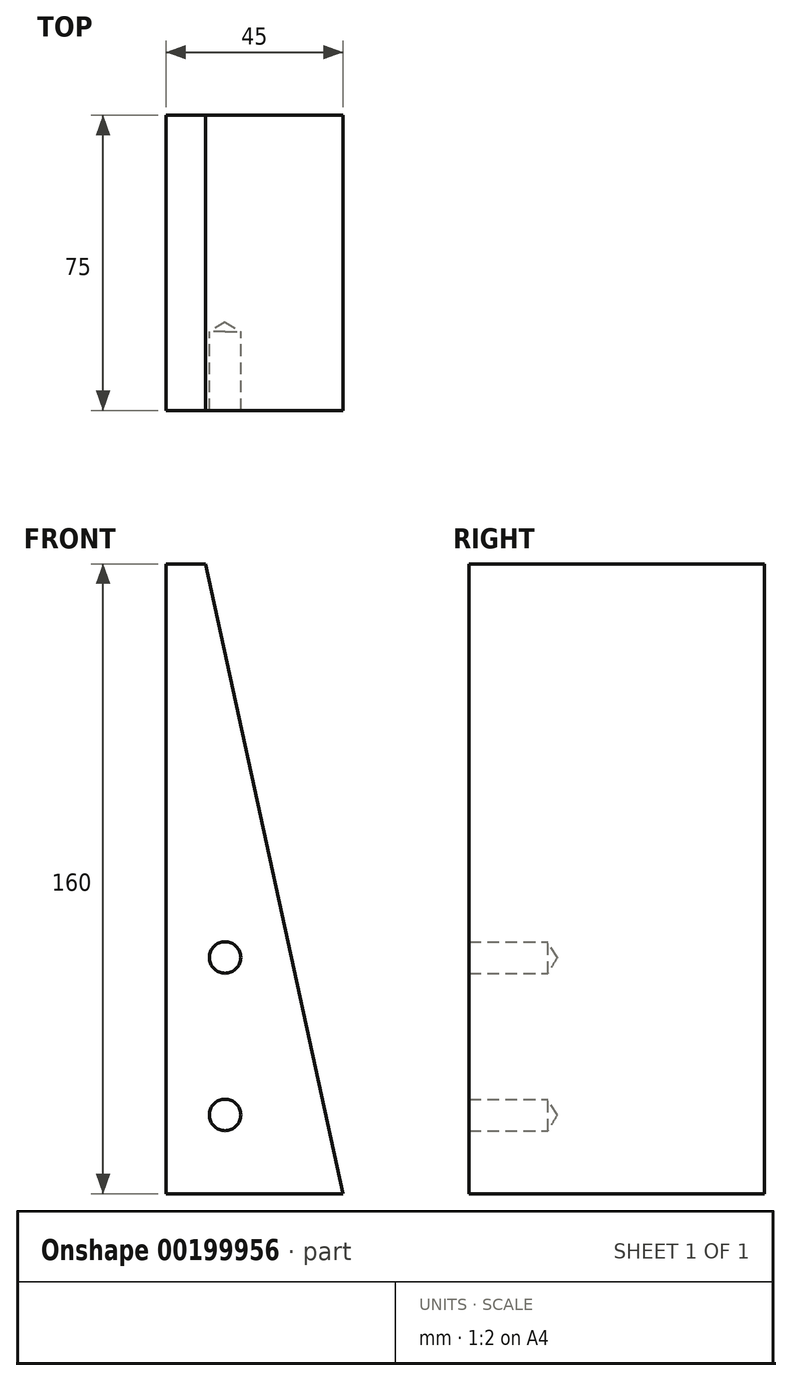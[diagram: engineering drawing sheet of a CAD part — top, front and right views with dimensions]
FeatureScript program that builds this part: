
annotation { "Feature Type Name" : "Feature", "Feature Type Description" : "" }
export const myFeature = defineFeature(function(context is Context, id is Id, definition is map)
    precondition{}
    {
        {
            var Q0;
            Q0=qCreatedBy(makeId("Front.planeOp"),FACE);
            var sketch = newSketch(context, id + "F0", { "sketchPlane" : qUnion([Q0])});
            skLineSegment(sketch, "E0", {"start": v(-41.7, 35.57) * mm, "end": v(-41.7, -124.43) * mm});
            skLineSegment(sketch, "E1", {"start": v(-41.7, -124.43) * mm, "end": v(3.3, -124.43) * mm});
            skLineSegment(sketch, "E2", {"start": v(3.3, -124.43) * mm, "end": v(-31.7, 35.57) * mm});
            skLineSegment(sketch, "E3", {"start": v(-31.7, 35.57) * mm, "end": v(-41.7, 35.57) * mm});
            skSolve(sketch);
        }
        {
            var Q0;
            Q0 = qSketchRegion(id + "F0", true);
            extrude(context, id + "F1", {"entities" : qUnion([Q0]), "depth" : 75 * mm});
        }
        {
            var Q0;
            Q0=makeQuery(id+"F1.opExtrude","CAP_FACE",FACE,{"disambiguationData":[OSD([sQuery(id+"F0.wireOp",EDGE,"E0"),sQuery(id+"F0.wireOp",EDGE,"E1"),sQuery(id+"F0.wireOp",EDGE,"E2"),sQuery(id+"F0.wireOp",EDGE,"E3")])],"isStart":false});
            var sketch = newSketch(context, id + "F2", { "sketchPlane" : qUnion([Q0])});
            skPoint(sketch, "E4", {"position": v(-26.7, -104.43) * mm});
            skPoint(sketch, "E5", {"position": v(-26.7, -64.43) * mm});
            skSolve(sketch);
        }
        {
            var Q0;
            Q0=sQuery(id+"F2.wireOp",VERTEX,"E5");
            var Q1;
            Q1=sQuery(id+"F2.wireOp",VERTEX,"E4");
            var Q2;
            Q2=makeQuery(id+"F1.opExtrude","SWEPT_BODY",BODY,{"disambiguationData":[OSD([sQuery(id+"F0.wireOp",EDGE,"E0"),sQuery(id+"F0.wireOp",EDGE,"E1"),sQuery(id+"F0.wireOp",EDGE,"E2"),sQuery(id+"F0.wireOp",EDGE,"E3")])]});
            hole(context, id + "F3", {"style" : HoleStyle.SIMPLE, "endStyle" : HoleEndStyle.BLIND, "holeDiameter" : 8 * mm, "holeDepth" : 20 * mm, "locations" : qUnion([Q0, Q1]), "scope" : qUnion([Q2])});
        }
    });
